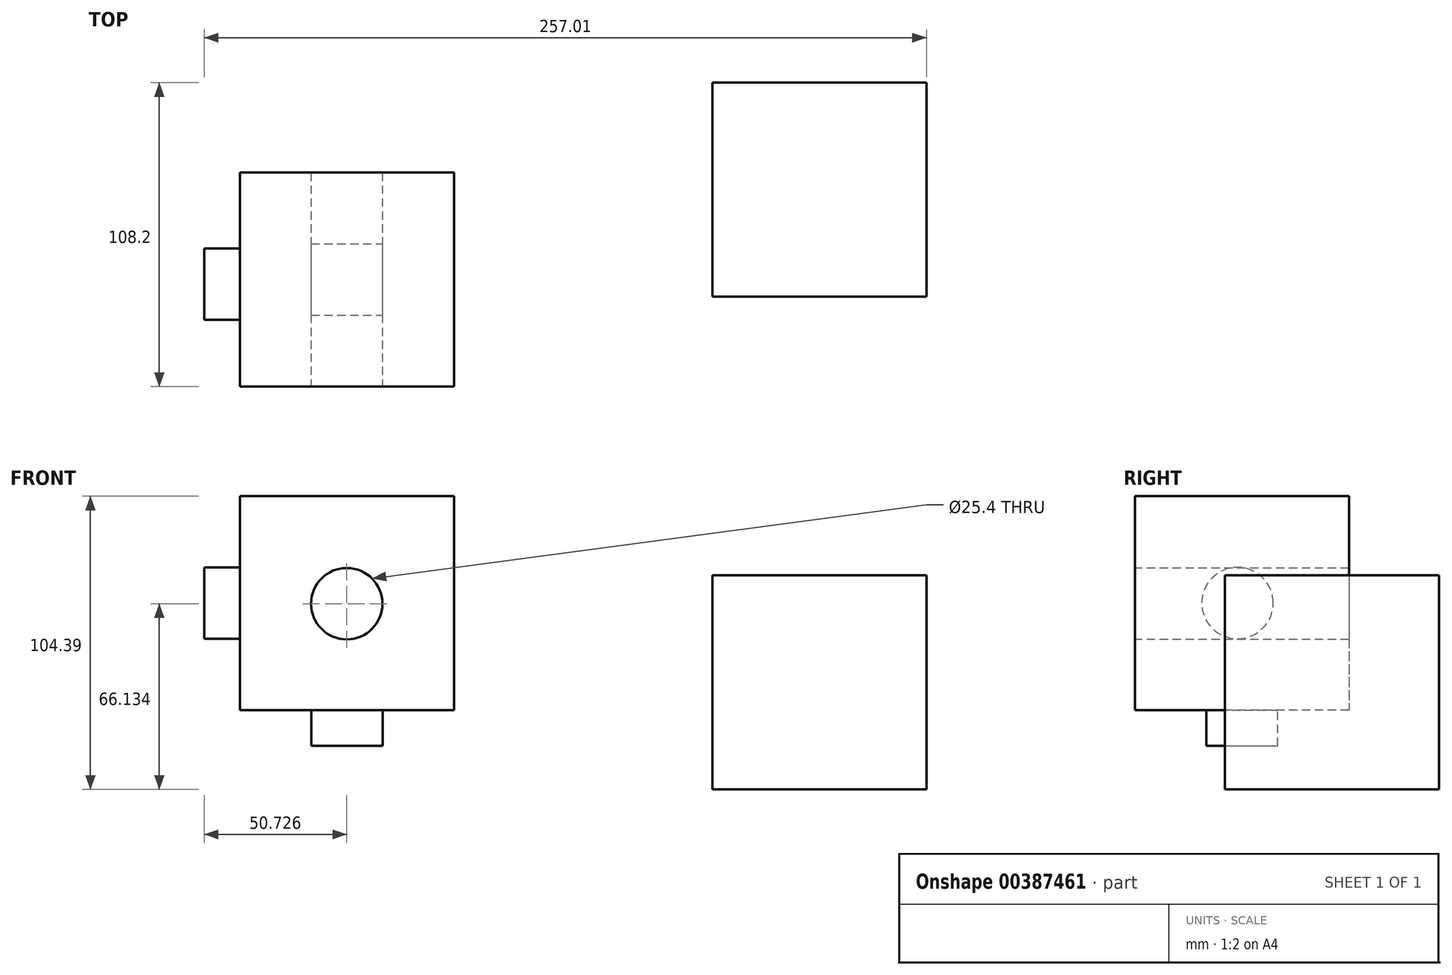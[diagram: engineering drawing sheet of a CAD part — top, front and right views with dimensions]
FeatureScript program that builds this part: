
annotation { "Feature Type Name" : "Feature", "Feature Type Description" : "" }
export const myFeature = defineFeature(function(context is Context, id is Id, definition is map)
    precondition{}
    {
        {
            var Q0;
            Q0=qCreatedBy(makeId("Top.planeOp"),FACE);
            var sketch = newSketch(context, id + "F0", { "sketchPlane" : qUnion([Q0])});
            skLineSegment(sketch, "E0.bottom", {"start": v(-168.11, -86.18) * mm, "end": v(-91.91, -86.18) * mm});
            skLineSegment(sketch, "E0.top", {"start": v(-168.11, -162.38) * mm, "end": v(-91.91, -162.38) * mm});
            skLineSegment(sketch, "E0.left", {"start": v(-168.11, -86.18) * mm, "end": v(-168.11, -162.38) * mm});
            skLineSegment(sketch, "E0.right", {"start": v(-91.91, -86.18) * mm, "end": v(-91.91, -162.38) * mm});
            skSolve(sketch);
        }
        {
            var Q0;
            Q0=makeQuery(id+"F0.imprint","IMPRINT",FACE,{"disambiguationData":[TD([[makeQuery(id+"F0.imprint","IMPRINT",EDGE,{"derivedFrom":sQuery(id+"F0.wireOp",EDGE,"E0.bottom")}),-1.0]])]});
            extrude(context, id + "F1", {"entities" : qUnion([Q0]), "depth" : 76.2 * mm});
        }
        {
            var Q0;
            Q0=makeQuery(id+"F1.opExtrude","CAP_FACE",FACE,{"disambiguationData":[OSD([sQuery(id+"F0.wireOp",EDGE,"E0.bottom"),sQuery(id+"F0.wireOp",EDGE,"E0.top"),sQuery(id+"F0.wireOp",EDGE,"E0.left"),sQuery(id+"F0.wireOp",EDGE,"E0.right")])],"isStart":true});
            var sketch = newSketch(context, id + "F2", { "sketchPlane" : qUnion([Q0])});
            skPoint(sketch, "E1", {"position": v(-130.01, 201.8) * mm});
            skPoint(sketch, "E1.positionSnap0", {"position": v(-130.01, 162.38) * mm});
            skSolve(sketch);
        }
        {
            var Q0;
            Q0=makeQuery(id+"F1.opExtrude","SWEPT_FACE",FACE,{"disambiguationData":[OSD([sQuery(id+"F0.wireOp",EDGE,"E0.top")])]});
            var sketch = newSketch(context, id + "F3", { "sketchPlane" : qUnion([Q0])});
            skPoint(sketch, "E2", {"position": v(-130.08, 37.94) * mm});
            skSolve(sketch);
        }
        {
            var Q0;
            Q0=sQuery(id+"F3.wireOp",VERTEX,"E2");
            var Q1;
            Q1=makeQuery(id+"F1.opExtrude","SWEPT_BODY",BODY,{"disambiguationData":[OSD([sQuery(id+"F0.wireOp",EDGE,"E0.bottom"),sQuery(id+"F0.wireOp",EDGE,"E0.top"),sQuery(id+"F0.wireOp",EDGE,"E0.left"),sQuery(id+"F0.wireOp",EDGE,"E0.right")])]});
            hole(context, id + "F4", {"style" : HoleStyle.SIMPLE, "endStyle" : HoleEndStyle.THROUGH, "holeDiameter" : 25.4 * mm, "isTappedThrough" : true, "tappedDepth" : 12.7 * mm, "tapClearance" : 3, "locations" : qUnion([Q0]), "scope" : qUnion([Q1])});
        }
        {
            var Q0;
            Q0=makeQuery(id+"F2.imprint","IMPRINT",FACE,{"disambiguationData":[TD([[makeQuery(id+"F2.imprint","IMPRINT",EDGE,{"derivedFrom":makeQuery(id+"F1.opExtrude","CAP_EDGE",EDGE,{"disambiguationData":[OSD([sQuery(id+"F0.wireOp",EDGE,"E0.bottom")])],"isStart":true})}),1.0]])]});
            var sketch = newSketch(context, id + "F5", { "sketchPlane" : qUnion([Q0])});
            skLineSegment(sketch, "E3.bottom", {"start": v(-142.71, 136.98) * mm, "end": v(-117.31, 136.98) * mm});
            skLineSegment(sketch, "E3.top", {"start": v(-142.71, 111.58) * mm, "end": v(-117.31, 111.58) * mm});
            skLineSegment(sketch, "E3.left", {"start": v(-142.71, 136.98) * mm, "end": v(-142.71, 111.58) * mm});
            skLineSegment(sketch, "E3.right", {"start": v(-117.31, 136.98) * mm, "end": v(-117.31, 111.58) * mm});
            skSolve(sketch);
        }
        {
            var Q0;
            Q0=makeQuery(id+"F5.imprint","IMPRINT",FACE,{"disambiguationData":[TD([[makeQuery(id+"F5.imprint","IMPRINT",EDGE,{"derivedFrom":sQuery(id+"F5.wireOp",EDGE,"E3.bottom")}),-1.0]])]});
            extrude(context, id + "F6", {"entities" : qUnion([Q0]), "operationType" : NewBodyOperationType.ADD, "depth" : 12.7 * mm});
        }
        {
            var Q0;
            Q0=makeQuery(id+"F1.opExtrude","SWEPT_FACE",FACE,{"disambiguationData":[OSD([sQuery(id+"F0.wireOp",EDGE,"E0.left")])]});
            var sketch = newSketch(context, id + "F7", { "sketchPlane" : qUnion([Q0])});
            skCircle(sketch, "E4", {"center": v(125.86, 38.2) * mm, "radius": 12.7 * mm});
            skSolve(sketch);
        }
        {
            var Q0;
            Q0=makeQuery(id+"F7.imprint","IMPRINT",FACE,{"disambiguationData":[TD([[makeQuery(id+"F7.imprint","IMPRINT",EDGE,{"derivedFrom":sQuery(id+"F7.wireOp",EDGE,"E4")}),1.0]])]});
            extrude(context, id + "F8", {"entities" : qUnion([Q0]), "operationType" : NewBodyOperationType.ADD, "depth" : 12.7 * mm});
        }
        {
            var Q0;
            Q0=qCreatedBy(makeId("Right.planeOp"),FACE);
            var sketch = newSketch(context, id + "F9", { "sketchPlane" : qUnion([Q0])});
            skLineSegment(sketch, "E5.bottom", {"start": v(-54.18, -28.2) * mm, "end": v(-130.38, -28.2) * mm});
            skLineSegment(sketch, "E5.top", {"start": v(-54.18, 48) * mm, "end": v(-130.38, 48) * mm});
            skLineSegment(sketch, "E5.left", {"start": v(-54.18, -28.2) * mm, "end": v(-54.18, 48) * mm});
            skLineSegment(sketch, "E5.right", {"start": v(-130.38, -28.2) * mm, "end": v(-130.38, 48) * mm});
            skSolve(sketch);
        }
        {
            var Q0;
            Q0=makeQuery(id+"F9.imprint","IMPRINT",FACE,{"disambiguationData":[TD([[makeQuery(id+"F9.imprint","IMPRINT",EDGE,{"derivedFrom":sQuery(id+"F9.wireOp",EDGE,"E5.bottom")}),-1.0]])]});
            extrude(context, id + "F10", {"entities" : qUnion([Q0]), "depth" : 76.2 * mm});
        }
    });
